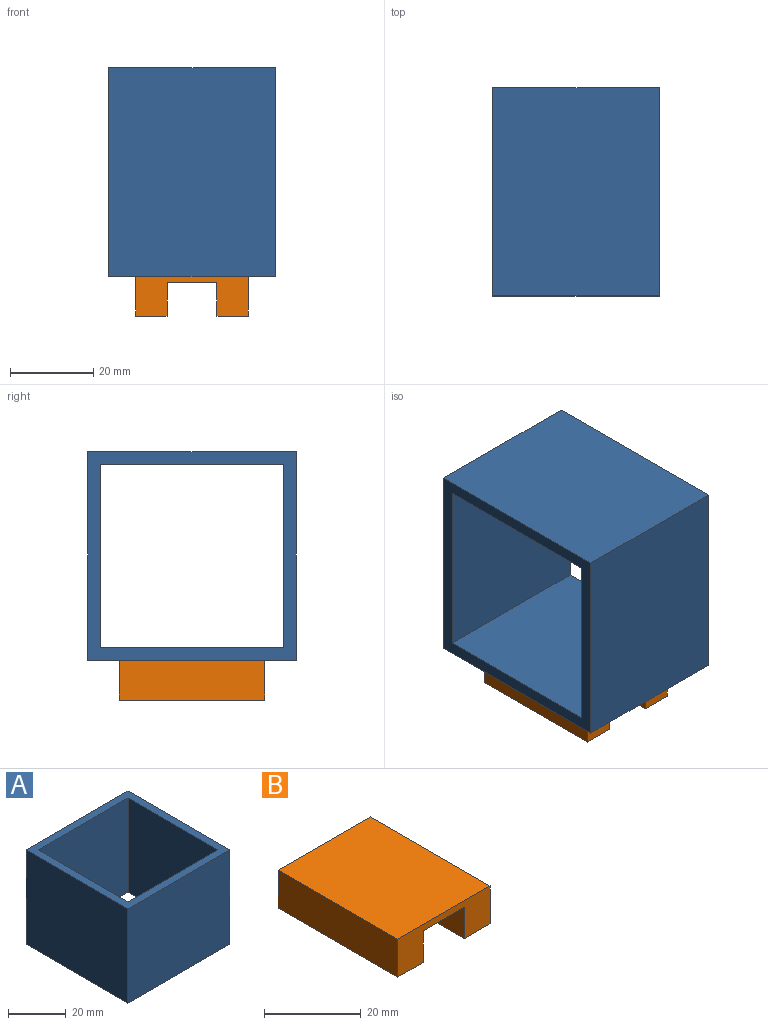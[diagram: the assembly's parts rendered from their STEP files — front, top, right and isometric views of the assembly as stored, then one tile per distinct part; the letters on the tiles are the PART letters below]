
ASSEMBLY  parts=2 mates=1
PART A: 10 faces, bbox 50x50x40 mm
  f0: plane 50x40mm, normal (0,-1,0), area 2000mm2, adj f1,f7,f8,f9
  f1: plane 50x40mm, normal (1,0,0), area 2000mm2, adj f0,f2,f8,f9
  f2: plane 50x40mm, normal (0,1,0), area 2000mm2, adj f1,f7,f8,f9
  f3: plane 44x40mm, normal (0,1,0), area 1760mm2, adj f4,f6,f8,f9
  f4: plane 44x40mm, normal (1,0,0), area 1760mm2, adj f3,f5,f8,f9
  f5: plane 44x40mm, normal (0,-1,0), area 1760mm2, adj f4,f6,f8,f9
  f6: plane 44x40mm, normal (-1,0,0), area 1760mm2, adj f3,f5,f8,f9
  f7: plane 50x40mm, normal (-1,0,0), area 2000mm2, adj f0,f2,f8,f9
  f8: plane 50x50mm, normal (0,0,1), area 564mm2, adj f0,f1,f2,f3,f4,f5,f6,f7
  f9: plane 50x50mm, normal (0,0,-1), area 564mm2, adj f0,f1,f2,f3,f4,f5,f6,f7
PART B: 10 faces, bbox 27x35x9.6 mm
  f0: plane 35x7.5mm, normal (0,0,-1), area 262.5mm2, adj f1,f7,f8,f9
  f1: plane 35x8mm, normal (1,0,0), area 280mm2, adj f0,f2,f8,f9
  f2: plane 35x12mm, normal (0,0,-1), area 420mm2, adj f1,f3,f8,f9
  f3: plane 35x8mm, normal (-1,0,0), area 280mm2, adj f2,f4,f8,f9
  f4: plane 35x7.5mm, normal (0,0,-1), area 262.5mm2, adj f3,f5,f8,f9
  f5: plane 35x9.6mm, normal (1,0,0), area 336mm2, adj f4,f6,f8,f9
  f6: plane 35x27mm, normal (0,0,1), area 945mm2, adj f5,f7,f8,f9
  f7: plane 35x9.6mm, normal (-1,0,0), area 336mm2, adj f0,f6,f8,f9
  f8: plane 27x9.6mm, normal (0,-1,0), area 163.2mm2, adj f0,f1,f2,f3,f4,f5,f6,f7
  f9: plane 27x9.6mm, normal (0,1,0), area 163.2mm2, adj f0,f1,f2,f3,f4,f5,f6,f7
PLACE A rot(axis=(0.58,0.58,0.58),120deg) t=(26.26,18.34,17.25)mm
PLACE B t=(46.26,435.84,-17.35)mm
MATE fastened A.f0 <-> B.f6  axis (0,0,-1) through (46.26,18.34,-7.75)mm
